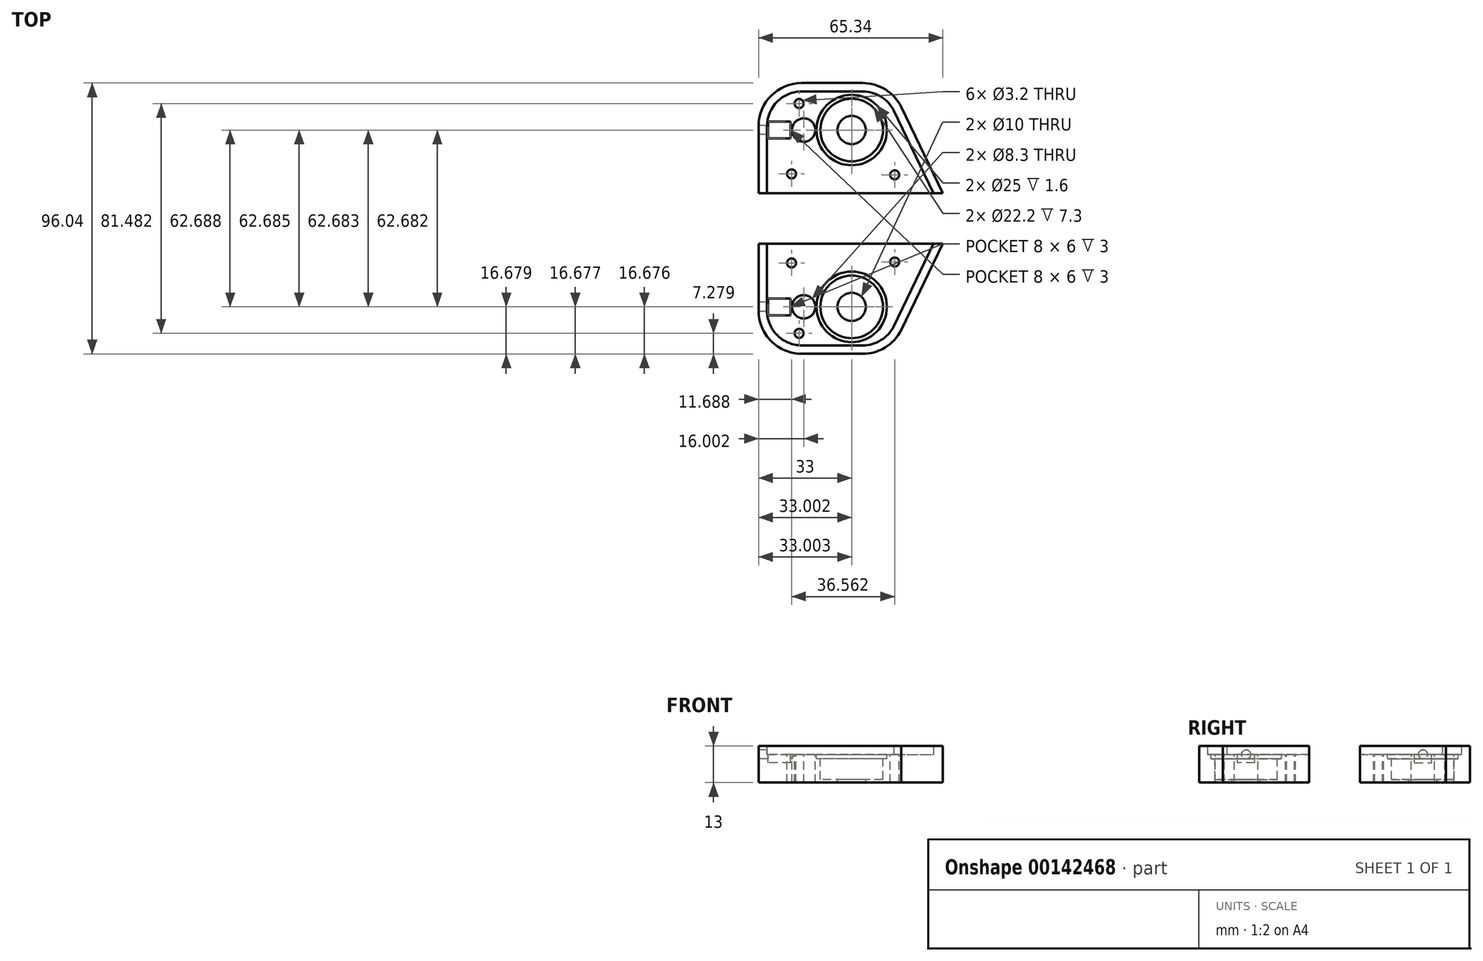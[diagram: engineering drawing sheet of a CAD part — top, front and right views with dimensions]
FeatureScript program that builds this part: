
annotation { "Feature Type Name" : "Feature", "Feature Type Description" : "" }
export const myFeature = defineFeature(function(context is Context, id is Id, definition is map)
    precondition{}
    {
        {
            var Q0;
            Q0=qCreatedBy(makeId("Top.planeOp"),FACE);
            var sketch = newSketch(context, id + "F0", { "sketchPlane" : qUnion([Q0])});
            skArc(sketch, "E0", {"start": v(-36.38, 15.84) * mm, "mid": v(-42.57, 11.51) * mm, "end": v(-44.95, 4.35) * mm});
            skLineSegment(sketch, "E1", {"start": v(-44.95, 4.35) * mm, "end": v(-44.95, 1.11) * mm});
            skLineSegment(sketch, "E2", {"start": v(-44.95, 1.11) * mm, "end": v(-35.81, 1.1) * mm});
            skArc(sketch, "E3", {"start": v(-35.81, 1.1) * mm, "mid": v(-35.56, 1.18) * mm, "end": v(-35.38, 1.36) * mm});
            skArc(sketch, "E4", {"start": v(-34.7, 0.68) * mm, "mid": v(-34.6, 1.46) * mm, "end": v(-35.38, 1.36) * mm});
            skArc(sketch, "E5", {"start": v(-34.7, 0.68) * mm, "mid": v(-34.88, 0.5) * mm, "end": v(-34.95, 0.24) * mm});
            skLineSegment(sketch, "E6", {"start": v(-34.95, 0.24) * mm, "end": v(-34.95, -1.32) * mm});
            skArc(sketch, "E7", {"start": v(-34.95, -1.32) * mm, "mid": v(-34.88, -1.57) * mm, "end": v(-34.7, -1.76) * mm});
            skArc(sketch, "E8", {"start": v(-35.38, -2.44) * mm, "mid": v(-34.6, -2.54) * mm, "end": v(-34.7, -1.76) * mm});
            skArc(sketch, "E9", {"start": v(-35.38, -2.44) * mm, "mid": v(-35.56, -2.26) * mm, "end": v(-35.81, -2.2) * mm});
            skLineSegment(sketch, "E10", {"start": v(-35.81, -2.2) * mm, "end": v(-44.95, -2.19) * mm});
            skLineSegment(sketch, "E11", {"start": v(-44.95, -2.19) * mm, "end": v(-44.95, -32.72) * mm});
            skArc(sketch, "E12", {"start": v(-44.95, -32.72) * mm, "mid": v(-41.43, -41.2) * mm, "end": v(-32.95, -44.72) * mm});
            skLineSegment(sketch, "E13", {"start": v(-32.95, -44.72) * mm, "end": v(-11.34, -44.72) * mm});
            skArc(sketch, "E14", {"start": v(-11.34, -44.72) * mm, "mid": v(-5.05, -42.93) * mm, "end": v(-0.62, -38.11) * mm});
            skCircle(sketch, "E15", {"center": v(-15.25, -31.35) * mm, "radius": 5 * mm});
            skCircle(sketch, "E16", {"center": v(-32.25, -31.34) * mm, "radius": 4 * mm, "construction": true});
            skCircle(sketch, "E17", {"center": v(-9.12, -0.54) * mm, "radius": 1.6 * mm});
            skLineSegment(sketch, "E18", {"start": v(31.53, 1.15) * mm, "end": v(43.05, 1.15) * mm});
            skLineSegment(sketch, "E19", {"start": v(43.05, 1.15) * mm, "end": v(43.05, 10.62) * mm});
            skArc(sketch, "E20", {"start": v(43.05, 10.62) * mm, "mid": v(42.77, 13.22) * mm, "end": v(41.93, 15.7) * mm});
            skLineSegment(sketch, "E21", {"start": v(41.93, 15.7) * mm, "end": v(31.53, 32.15) * mm});
            skLineSegment(sketch, "E22", {"start": v(31.53, 32.15) * mm, "end": v(28.44, 32.15) * mm});
            skLineSegment(sketch, "E23", {"start": v(16.7, -2.2) * mm, "end": v(16.7, 0.29) * mm});
            skArc(sketch, "E24", {"start": v(16.7, 0.29) * mm, "mid": v(16.64, 0.54) * mm, "end": v(16.45, 0.72) * mm});
            skArc(sketch, "E25", {"start": v(17.14, 1.4) * mm, "mid": v(16.35, 1.5) * mm, "end": v(16.45, 0.72) * mm});
            skArc(sketch, "E26", {"start": v(17.14, 1.4) * mm, "mid": v(17.32, 1.22) * mm, "end": v(17.57, 1.15) * mm});
            skLineSegment(sketch, "E27", {"start": v(17.57, 1.15) * mm, "end": v(28.23, 1.15) * mm});
            skLineSegment(sketch, "E28", {"start": v(28.23, 1.15) * mm, "end": v(28.23, 10.94) * mm});
            skArc(sketch, "E29", {"start": v(28.23, 10.94) * mm, "mid": v(28.16, 11.19) * mm, "end": v(27.98, 11.37) * mm});
            skArc(sketch, "E30", {"start": v(28.66, 12.05) * mm, "mid": v(27.87, 12.16) * mm, "end": v(27.98, 11.37) * mm});
            skArc(sketch, "E31", {"start": v(28.66, 12.05) * mm, "mid": v(28.84, 11.87) * mm, "end": v(29.1, 11.8) * mm});
            skLineSegment(sketch, "E32", {"start": v(29.1, 11.8) * mm, "end": v(30.66, 11.8) * mm});
            skArc(sketch, "E33", {"start": v(30.66, 11.8) * mm, "mid": v(30.91, 11.87) * mm, "end": v(31.1, 12.05) * mm});
            skArc(sketch, "E34", {"start": v(31.78, 11.37) * mm, "mid": v(31.88, 12.16) * mm, "end": v(31.1, 12.05) * mm});
            skArc(sketch, "E35", {"start": v(31.78, 11.37) * mm, "mid": v(31.6, 11.19) * mm, "end": v(31.53, 10.94) * mm});
            skLineSegment(sketch, "E36", {"start": v(31.53, 10.94) * mm, "end": v(31.53, 1.15) * mm});
            skCircle(sketch, "E37", {"center": v(29.88, 21.8) * mm, "radius": 1.6 * mm});
            skLineSegment(sketch, "E38", {"start": v(28.44, 32.15) * mm, "end": v(-36.38, 15.84) * mm});
            skLineSegment(sketch, "E39", {"start": v(-0.62, -38.11) * mm, "end": v(16.7, -2.2) * mm});
            skSolve(sketch);
        }
        {
            var Q0;
            Q0=makeQuery(id+"F0.imprint","IMPRINT",FACE,{"disambiguationData":[TD([[makeQuery(id+"F0.imprint","IMPRINT",EDGE,{"derivedFrom":sQuery(id+"F0.wireOp",EDGE,"E0")}),1.0]])]});
            var sketch = newSketch(context, id + "F1", { "sketchPlane" : qUnion([Q0])});
            skLineSegment(sketch, "E40.0", {"start": v(2.34, -39.57) * mm, "end": v(17.1, -8.99) * mm});
            skLineSegment(sketch, "E40.1", {"start": v(-48.25, -8.99) * mm, "end": v(-48.25, -32.72) * mm});
            skArc(sketch, "E40.2", {"start": v(-48.25, -32.72) * mm, "mid": v(-43.77, -43.53) * mm, "end": v(-32.95, -48.02) * mm});
            skLineSegment(sketch, "E40.3", {"start": v(-32.95, -48.02) * mm, "end": v(-11.34, -48.02) * mm});
            skArc(sketch, "E40.4", {"start": v(-11.34, -48.02) * mm, "mid": v(-3.3, -45.73) * mm, "end": v(2.34, -39.57) * mm});
            skLineSegment(sketch, "E41.0", {"start": v(-0.35, -38.25) * mm, "end": v(13.76, -8.99) * mm});
            skLineSegment(sketch, "E41.1", {"start": v(-45.25, -8.99) * mm, "end": v(-45.25, -32.72) * mm});
            skArc(sketch, "E41.2", {"start": v(-45.25, -32.72) * mm, "mid": v(-41.65, -41.41) * mm, "end": v(-32.95, -45.02) * mm});
            skLineSegment(sketch, "E41.3", {"start": v(-32.95, -45.02) * mm, "end": v(-11.34, -45.02) * mm});
            skArc(sketch, "E41.4", {"start": v(-11.34, -45.02) * mm, "mid": v(-4.89, -43.19) * mm, "end": v(-0.35, -38.25) * mm});
            skLineSegment(sketch, "E42", {"start": v(-48.25, -8.99) * mm, "end": v(17.1, -8.99) * mm});
            skLineSegment(sketch, "E43", {"start": v(-32.26, -31.34) * mm, "end": v(-48.25, -31.34) * mm, "construction": true});
            skSolve(sketch);
        }
        {
            var Q0;
            Q0 = qSketchRegion(id + "F1", true);
            extrude(context, id + "F2", {"entities" : qUnion([Q0]), "oppositeDirection" : true, "depth" : 10 * mm});
        }
        {
            var Q0;
            {var subQ0=sQuery(id+"F1.wireOp",EDGE,"E40.0");Q0=makeQuery(id+"F1.imprint","IMPRINT",FACE,{"disambiguationData":[TD([[makeQuery(id+"F1.imprint","IMPRINT",EDGE,{"derivedFrom":subQ0}),1.0]])]});}
            extrude(context, id + "F3", {"entities" : qUnion([Q0]), "operationType" : NewBodyOperationType.ADD, "depth" : 3 * mm});
        }
        {
            var Q0;
            Q0=makeQuery(id+"F0.imprint","IMPRINT",FACE,{"disambiguationData":[TD([[makeQuery(id+"F0.imprint","IMPRINT",EDGE,{"derivedFrom":sQuery(id+"F0.wireOp",EDGE,"E0")}),1.0]])]});
            var sketch = newSketch(context, id + "F4", { "sketchPlane" : qUnion([Q0])});
            skCircle(sketch, "E44", {"center": v(-32.25, -31.34) * mm, "radius": 4.15 * mm});
            skSolve(sketch);
        }
        {
            var Q0;
            Q0 = qSketchRegion(id + "F4", true);
            extrude(context, id + "F5", {"entities" : qUnion([Q0]), "operationType" : NewBodyOperationType.REMOVE, "endBound" : BoundingType.THROUGH_ALL, "oppositeDirection" : true, "depth" : 25 * mm});
        }
        {
            var Q0;
            Q0=makeQuery(id+"F0.imprint","IMPRINT",FACE,{"disambiguationData":[TD([[makeQuery(id+"F0.imprint","IMPRINT",EDGE,{"derivedFrom":sQuery(id+"F0.wireOp",EDGE,"E15")}),-1.0]])]});
            var sketch = newSketch(context, id + "F6", { "sketchPlane" : qUnion([Q0])});
            skCircle(sketch, "E45", {"center": v(-15.25, -31.34) * mm, "radius": 5 * mm});
            skSolve(sketch);
        }
        {
            var Q0;
            Q0 = qSketchRegion(id + "F6", true);
            extrude(context, id + "F7", {"entities" : qUnion([Q0]), "operationType" : NewBodyOperationType.REMOVE, "endBound" : BoundingType.THROUGH_ALL, "oppositeDirection" : true, "depth" : 25 * mm});
        }
        {
            var Q0;
            Q0=makeQuery(id+"F0.imprint","IMPRINT",FACE,{"disambiguationData":[TD([[makeQuery(id+"F0.imprint","IMPRINT",EDGE,{"derivedFrom":sQuery(id+"F0.wireOp",EDGE,"E0")}),1.0]])]});
            var sketch = newSketch(context, id + "F8", { "sketchPlane" : qUnion([Q0])});
            skCircle(sketch, "E46", {"center": v(-15.25, -31.34) * mm, "radius": 12.5 * mm});
            skSolve(sketch);
        }
        {
            var Q0;
            Q0 = qSketchRegion(id + "F8", true);
            extrude(context, id + "F9", {"entities" : qUnion([Q0]), "operationType" : NewBodyOperationType.REMOVE, "oppositeDirection" : true, "depth" : 1.6 * mm});
        }
        {
            var Q0;
            Q0=makeQuery(id+"F0.imprint","IMPRINT",FACE,{"disambiguationData":[TD([[makeQuery(id+"F0.imprint","IMPRINT",EDGE,{"derivedFrom":sQuery(id+"F0.wireOp",EDGE,"E15")}),-1.0]])]});
            var sketch = newSketch(context, id + "F10", { "sketchPlane" : qUnion([Q0])});
            skCircle(sketch, "E47", {"center": v(-15.25, -31.34) * mm, "radius": 11.1 * mm});
            skSolve(sketch);
        }
        {
            var Q0;
            Q0 = qSketchRegion(id + "F10", true);
            extrude(context, id + "F11", {"entities" : qUnion([Q0]), "operationType" : NewBodyOperationType.REMOVE, "oppositeDirection" : true, "depth" : 8.9 * mm});
        }
        {
            var Q0;
            {var subQ0=sQuery(id+"F1.wireOp",EDGE,"E40.1");Q0=makeQuery(id+"F3.boolean.opBoolean","MERGE",FACE,{"derivedFrom":[makeQuery(id+"F2.opExtrude","SWEPT_FACE",FACE,{"disambiguationData":[OSD([subQ0])]}),makeQuery(id+"F3.opExtrude","SWEPT_FACE",FACE,{"disambiguationData":[OSD([subQ0])]})]});}
            var sketch = newSketch(context, id + "F12", { "sketchPlane" : qUnion([Q0])});
            skCircle(sketch, "E48", {"center": v(31.34, 0) * mm, "radius": 1.63 * mm});
            skSolve(sketch);
        }
        {
            var Q0;
            Q0 = qSketchRegion(id + "F12", true);
            extrude(context, id + "F13", {"entities" : qUnion([Q0]), "operationType" : NewBodyOperationType.REMOVE, "oppositeDirection" : true, "depth" : 14 * mm});
        }
        {
            var Q0;
            {var subQ0=makeQuery(id+"F0.imprint","IMPRINT",EDGE,{"derivedFrom":sQuery(id+"F0.wireOp",EDGE,"E12")});Q0=makeQuery(id+"F1.imprint","IMPRINT",FACE,{"disambiguationData":[TD([[makeQuery(id+"F1.imprint","IMPRINT",EDGE,{"derivedFrom":subQ0}),1.0]])]});}
            var sketch = newSketch(context, id + "F14", { "sketchPlane" : qUnion([Q0])});
            skLineSegment(sketch, "E49.bottom", {"start": v(-36.87, -28.37) * mm, "end": v(-44.87, -28.37) * mm});
            skLineSegment(sketch, "E49.top", {"start": v(-36.87, -34.37) * mm, "end": v(-44.87, -34.37) * mm});
            skLineSegment(sketch, "E49.left", {"start": v(-36.87, -28.37) * mm, "end": v(-36.87, -34.37) * mm});
            skLineSegment(sketch, "E49.right", {"start": v(-44.87, -28.37) * mm, "end": v(-44.87, -34.37) * mm});
            skPoint(sketch, "E49.middle", {"position": v(-40.87, -31.37) * mm});
            skSolve(sketch);
        }
        {
            var Q0;
            Q0 = qSketchRegion(id + "F14", true);
            extrude(context, id + "F15", {"entities" : qUnion([Q0]), "operationType" : NewBodyOperationType.REMOVE, "oppositeDirection" : true, "depth" : 3 * mm});
        }
        {
            var Q0;
            {var subQ0=makeQuery(id+"F0.imprint","IMPRINT",EDGE,{"derivedFrom":sQuery(id+"F0.wireOp",EDGE,"E12")});Q0=makeQuery(id+"F1.imprint","IMPRINT",FACE,{"disambiguationData":[TD([[makeQuery(id+"F1.imprint","IMPRINT",EDGE,{"derivedFrom":subQ0}),1.0]])]});}
            var sketch = newSketch(context, id + "F16", { "sketchPlane" : qUnion([Q0])});
            skCircle(sketch, "E50", {"center": v(-36.56, -15.78) * mm, "radius": 1.6 * mm});
            skCircle(sketch, "E51", {"center": v(0, -15.45) * mm, "radius": 1.6 * mm});
            skCircle(sketch, "E52", {"center": v(-33.87, -40.74) * mm, "radius": 1.6 * mm});
            skSolve(sketch);
        }
        {
            var Q0;
            Q0 = qSketchRegion(id + "F16", true);
            extrude(context, id + "F17", {"entities" : qUnion([Q0]), "operationType" : NewBodyOperationType.REMOVE, "endBound" : BoundingType.THROUGH_ALL, "oppositeDirection" : true, "depth" : 25 * mm});
        }
        {
            var Q0;
            Q0=makeQuery(id+"F2.opExtrude","SWEPT_BODY",BODY,{"disambiguationData":[OSD([sQuery(id+"F1.wireOp",EDGE,"E40.0"),sQuery(id+"F1.wireOp",EDGE,"E40.1"),sQuery(id+"F1.wireOp",EDGE,"E40.2"),sQuery(id+"F1.wireOp",EDGE,"E40.3"),sQuery(id+"F1.wireOp",EDGE,"E40.4"),sQuery(id+"F1.wireOp",EDGE,"E42")])]});
            var Q1;
            Q1=qCreatedBy(makeId("Front.planeOp"),FACE);
            mirror(context, id + "F18", {"entities" : qUnion([Q0]), "mirrorPlane" : qUnion([Q1])});
        }
    });
